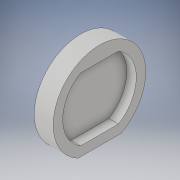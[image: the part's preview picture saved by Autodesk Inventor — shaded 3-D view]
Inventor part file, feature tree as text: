
AUTODESK INVENTOR PART (.ipt)
format: ipt  version: 2017 (Build 210142000, 142)  size: 114,176 bytes
history: native  units: in
note: dims shown in document units (in); Inventor stores cm internally (conversion verified against a paired STEP export)
features: extrude x2, sketch x2
ambient origin geometry x8: Origin, YZ Plane, XZ Plane, XY Plane, X Axis, Y Axis, Z Axis, Center Point
bodies: Body1 (feature_tree)
feature tree (4):
  extrude  "Extrusion4"  Depth=1.0in TaperAngle=0.0deg
  extrude  "Extrusion5"  Depth=1.0in
  sketch  "Sketch1"  dims[d12=6.6667in d13=4.0in d14=1.0in d15=0.0in]
  sketch  "Sketch5"  dims[d16=1.0in d17=0.0in d18=1.0in]
